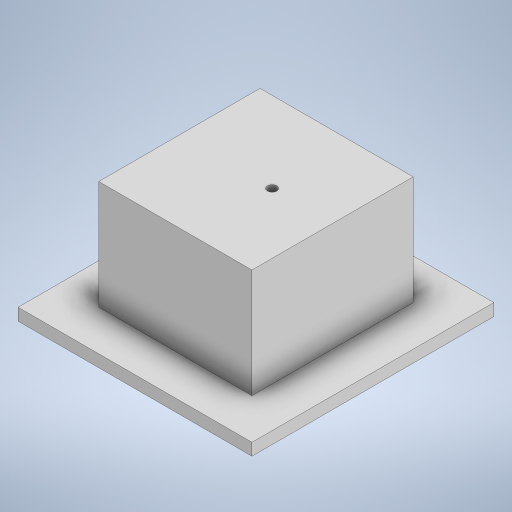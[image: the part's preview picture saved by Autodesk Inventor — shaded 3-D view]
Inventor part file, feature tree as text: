
AUTODESK INVENTOR PART (.ipt)
format: ipt  version: 2024 (Build 280153000, 153)  size: 274,944 bytes
history: native  units: mm
features: extrude x5, sketch x5, plane x3
ambient origin geometry x8: Origin, YZ Plane, XZ Plane, XY Plane, X Axis, Y Axis, Z Axis, Center Point
bodies: Body1 (feature_tree)
feature tree (13):
  plane  "Work Plane5"
  extrude  "Extrusion34"  Depth=40.0mm
  plane  "Work Plane2"
  extrude  "Extrusion35"  Depth=30.0mm
  plane  "Work Plane1"
  extrude  "Extrusion51"  Depth=30.0mm
  sketch  "Sketch77"  dims[d211=10.0mm d212=0.0mm d219=35.0mm]
  extrude  "Extrusion53"  Depth=10.0mm
  extrude  "Extrusion54"  Depth=60.0mm
  sketch  "Sketch45"  dims[d142=38.0mm d143=40.0mm]
  sketch  "Sketch47"  dims[d144=30.0mm d145=0.0mm d146=36.0mm]
  sketch  "Sketch74"  dims[d147=30.0mm d148=-2.617994mm d210=2.3mm]
  sketch  "Sketch78"  dims[d220=58.0mm d221=60.0mm d222=3.0mm d223=0.0mm d224=3.0mm d225=0.0mm d49=0.5mm d50=0.872665mm d51=0.5mm d52=0.872665mm d130=0.5mm d131=0.872665mm d132=0.5mm d133=0.872665mm d156=0.5mm d157=0.872665mm d158=0.5mm d159=0.872665mm d173=0.5mm d174=0.872665mm d175=0.5mm d176=0.872665mm d226=0.5mm d227=0.872665mm]
